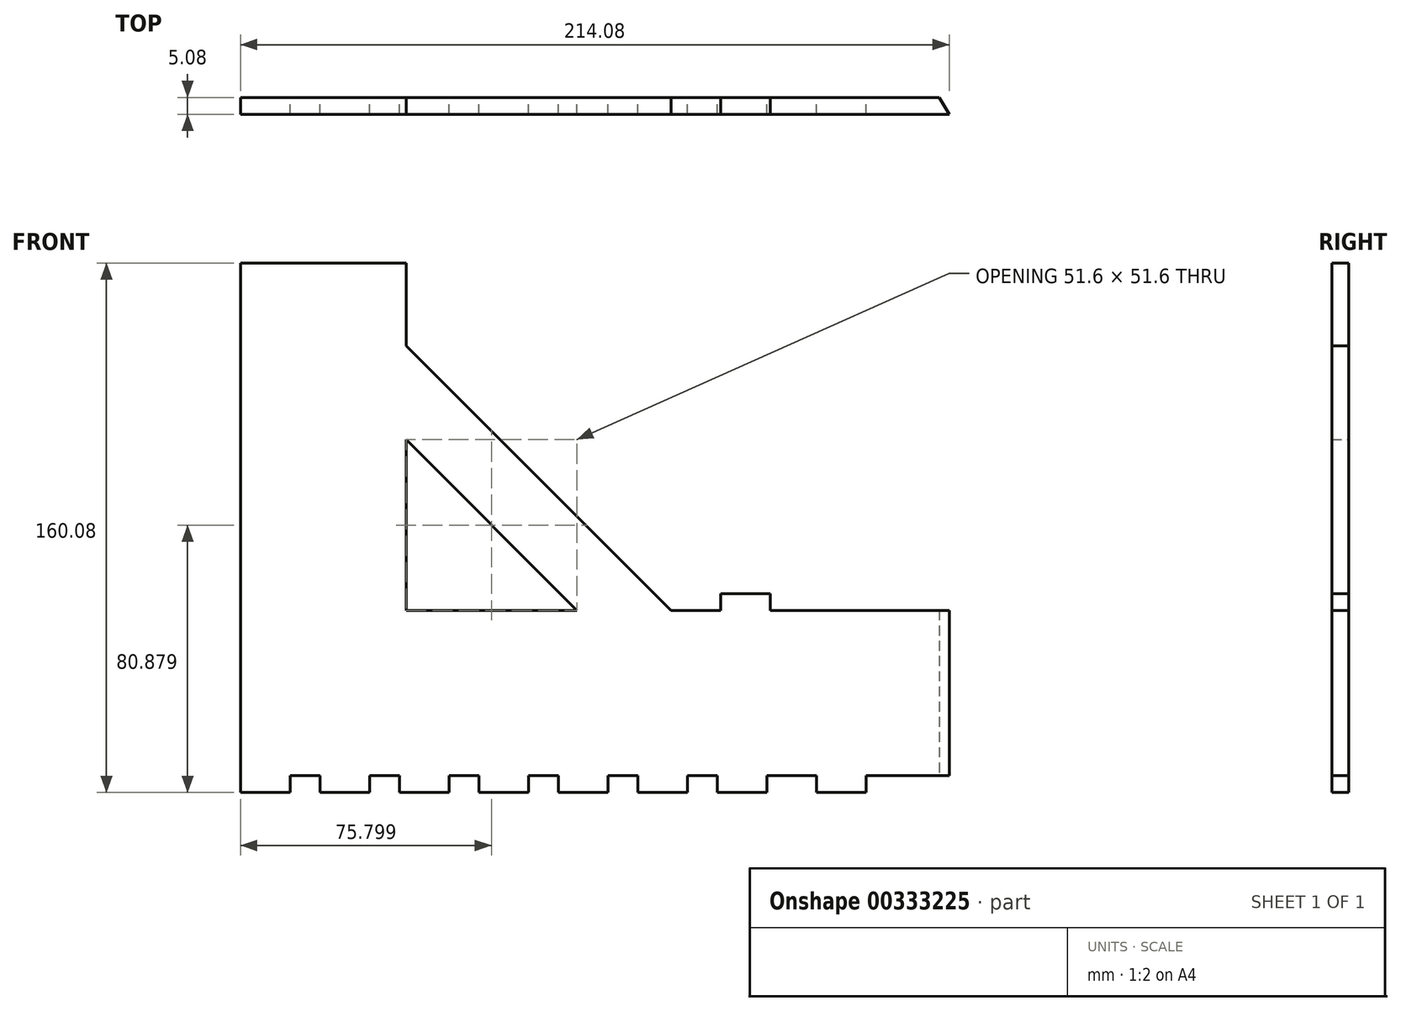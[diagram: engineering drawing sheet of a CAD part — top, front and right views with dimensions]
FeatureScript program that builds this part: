
annotation { "Feature Type Name" : "Feature", "Feature Type Description" : "" }
export const myFeature = defineFeature(function(context is Context, id is Id, definition is map)
    precondition{}
    {
        {
            var Q0;
            Q0=qCreatedBy(makeId("Front.planeOp"),FACE);
            var sketch = newSketch(context, id + "F0", { "sketchPlane" : qUnion([Q0])});
            skLineSegment(sketch, "E0", {"start": v(-32.42, 0) * mm, "end": v(-246.5, 0) * mm});
            skLineSegment(sketch, "E1", {"start": v(-246.5, 0) * mm, "end": v(-246.5, 130) * mm});
            skLineSegment(sketch, "E2", {"start": v(-246.5, 130) * mm, "end": v(-196.5, 130) * mm});
            skLineSegment(sketch, "E3", {"start": v(-196.5, 130) * mm, "end": v(-196.5, 50) * mm});
            skLineSegment(sketch, "E4", {"start": v(-196.5, 50) * mm, "end": v(-32.42, 50) * mm});
            skLineSegment(sketch, "E5", {"start": v(-196.5, 130) * mm, "end": v(-116.5, 50) * mm});
            skLineSegment(sketch, "E6", {"start": v(-196.5, 101.6) * mm, "end": v(-144.9, 50) * mm});
            skLineSegment(sketch, "E7", {"start": v(-246.5, 0) * mm, "end": v(-246.5, -5.08) * mm});
            skLineSegment(sketch, "E8", {"start": v(-246.5, -5.08) * mm, "end": v(-231.5, -5.08) * mm});
            skLineSegment(sketch, "E9", {"start": v(-231.5, -5.08) * mm, "end": v(-231.5, 0) * mm});
            skLineSegment(sketch, "E10.1.0.0", {"start": v(-207.5, -5.08) * mm, "end": v(-207.5, 0) * mm});
            skLineSegment(sketch, "E10.1.0.1", {"start": v(-222.5, -5.08) * mm, "end": v(-207.5, -5.08) * mm});
            skLineSegment(sketch, "E10.1.0.2", {"start": v(-222.5, 0) * mm, "end": v(-222.5, -5.08) * mm});
            skLineSegment(sketch, "E10.2.0.0", {"start": v(-183.5, -5.08) * mm, "end": v(-183.5, 0) * mm});
            skLineSegment(sketch, "E10.2.0.1", {"start": v(-198.5, -5.08) * mm, "end": v(-183.5, -5.08) * mm});
            skLineSegment(sketch, "E10.2.0.2", {"start": v(-198.5, 0) * mm, "end": v(-198.5, -5.08) * mm});
            skLineSegment(sketch, "E10.3.0.0", {"start": v(-159.5, -5.08) * mm, "end": v(-159.5, 0) * mm});
            skLineSegment(sketch, "E10.3.0.1", {"start": v(-174.5, -5.08) * mm, "end": v(-159.5, -5.08) * mm});
            skLineSegment(sketch, "E10.3.0.2", {"start": v(-174.5, 0) * mm, "end": v(-174.5, -5.08) * mm});
            skLineSegment(sketch, "E10.4.0.0", {"start": v(-135.5, -5.08) * mm, "end": v(-135.5, 0) * mm});
            skLineSegment(sketch, "E10.4.0.1", {"start": v(-150.5, -5.08) * mm, "end": v(-135.5, -5.08) * mm});
            skLineSegment(sketch, "E10.4.0.2", {"start": v(-150.5, 0) * mm, "end": v(-150.5, -5.08) * mm});
            skLineSegment(sketch, "E10.5.0.0", {"start": v(-111.5, -5.08) * mm, "end": v(-111.5, 0) * mm});
            skLineSegment(sketch, "E10.5.0.1", {"start": v(-126.5, -5.08) * mm, "end": v(-111.5, -5.08) * mm});
            skLineSegment(sketch, "E10.5.0.2", {"start": v(-126.5, 0) * mm, "end": v(-126.5, -5.08) * mm});
            skLineSegment(sketch, "E10.6.0.0", {"start": v(-87.5, -5.08) * mm, "end": v(-87.5, 0) * mm});
            skLineSegment(sketch, "E10.6.0.1", {"start": v(-102.5, -5.08) * mm, "end": v(-87.5, -5.08) * mm});
            skLineSegment(sketch, "E10.6.0.2", {"start": v(-102.5, 0) * mm, "end": v(-102.5, -5.08) * mm});
            skLineSegment(sketch, "E10.direction1", {"start": v(-246.5, -5.08) * mm, "end": v(-222.5, -5.08) * mm, "construction": true});
            skLineSegment(sketch, "E11", {"start": v(-32.42, 50) * mm, "end": v(-32.42, 0) * mm});
            skPoint(sketch, "E12.start.orphan", {"position": v(0, 50) * mm});
            skSolve(sketch);
        }
        {
            var Q0;
            Q0=qSketchRegion(id+"F0",true);
            extrude(context, id + "F1", {"entities" : qUnion([Q0]), "depth" : 5.08 * mm});
        }
        {
            var Q0;
            Q0=makeQuery(id+"F1.opExtrude","SWEPT_FACE",FACE,{"disambiguationData":[OSD([sQuery(id+"F0.wireOp",EDGE,"E2")])]});
            var Q1;
            Q1=makeQuery(id+"F1.opExtrude","SWEPT_FACE",FACE,{"disambiguationData":[OSD([sQuery(id+"F0.wireOp",EDGE,"0f3f7d79-0024-4810-854d-b7a6c9fa19c64.MirrorCS")])]});
            extrude(context, id + "F2", {"entities" : qUnion([Q0, Q1]), "operationType" : NewBodyOperationType.ADD, "depth" : 25 * mm});
        }
        {
            var Q0;
            {var subQ0=sQuery(id+"F0.wireOp",EDGE,"E0");Q0=makeQuery(id+"F1.opExtrude","SWEPT_FACE",FACE,{"disambiguationData":[OSD([subQ0]),TDD([makeQuery(id+"F0.imprint","IMPRINT",EDGE,{"disambiguationData":[TD([[makeQuery(id+"F0.imprint","INTERSECT",VERTEX,{"derivedFrom":[subQ0,sQuery(id+"F0.wireOp",EDGE,"E11")]}),-1.0]])],"derivedFrom":subQ0})])]});}
            var sketch = newSketch(context, id + "F3", { "sketchPlane" : qUnion([Q0])});
            skLineSegment(sketch, "E13", {"start": v(-32.42, 5.08) * mm, "end": v(-35.35, 0) * mm});
            skSolve(sketch);
        }
        {
            var Q0;
            {var subQ0=sQuery(id+"F3.wireOp",EDGE,"E13");Q0=makeQuery(id+"F3.imprint","IMPRINT",FACE,{"disambiguationData":[TD([[makeQuery(id+"F3.imprint","IMPRINT",EDGE,{"derivedFrom":subQ0}),1.0]])]});}
            extrude(context, id + "F4", {"entities" : qUnion([Q0]), "operationType" : NewBodyOperationType.REMOVE, "oppositeDirection" : true, "depth" : 58 * mm});
        }
        {
            var Q0;
            {var subQ0=sQuery(id+"F0.wireOp",EDGE,"E0");Q0=makeQuery(id+"F1.opExtrude","SWEPT_FACE",FACE,{"disambiguationData":[OSD([subQ0]),TDD([makeQuery(id+"F0.imprint","IMPRINT",EDGE,{"disambiguationData":[TD([[makeQuery(id+"F0.imprint","INTERSECT",VERTEX,{"derivedFrom":[subQ0,sQuery(id+"F0.wireOp",EDGE,"E11")]}),-1.0]])],"derivedFrom":subQ0})])]});}
            var sketch = newSketch(context, id + "F5", { "sketchPlane" : qUnion([Q0])});
            skLineSegment(sketch, "E14.bottom", {"start": v(-72.5, 5.08) * mm, "end": v(-57.5, 5.08) * mm});
            skLineSegment(sketch, "E14.top", {"start": v(-72.5, 0) * mm, "end": v(-57.5, 0) * mm});
            skLineSegment(sketch, "E14.right", {"start": v(-57.5, 5.08) * mm, "end": v(-57.5, 0) * mm});
            skLineSegment(sketch, "E15", {"start": v(-72.5, 5.08) * mm, "end": v(-72.5, 0) * mm});
            skPoint(sketch, "E14.left.start.orphan", {"position": v(-87.5, 5.08) * mm});
            skPoint(sketch, "E16.orphan", {"position": v(-87.5, 0) * mm});
            skSolve(sketch);
        }
        {
            var Q0;
            Q0=qSketchRegion(id+"F5",true);
            extrude(context, id + "F6", {"entities" : qUnion([Q0]), "operationType" : NewBodyOperationType.ADD, "depth" : 5.08 * mm});
        }
        {
            var Q0;
            {var subQ0=sQuery(id+"F0.wireOp",EDGE,"E4");Q0=makeQuery(id+"F1.opExtrude","SWEPT_FACE",FACE,{"disambiguationData":[OSD([subQ0]),TDD([makeQuery(id+"F0.imprint","IMPRINT",EDGE,{"disambiguationData":[TD([[makeQuery(id+"F0.imprint","INTERSECT",VERTEX,{"derivedFrom":[subQ0,sQuery(id+"F0.wireOp",EDGE,"E11")]}),1.0]])],"derivedFrom":subQ0})])]});}
            var sketch = newSketch(context, id + "F7", { "sketchPlane" : qUnion([Q0])});
            skLineSegment(sketch, "E17.bottom", {"start": v(-101.5, 0) * mm, "end": v(-86.5, 0) * mm});
            skLineSegment(sketch, "E17.top", {"start": v(-101.5, -5.08) * mm, "end": v(-86.5, -5.08) * mm});
            skLineSegment(sketch, "E17.right", {"start": v(-86.5, 0) * mm, "end": v(-86.5, -5.08) * mm});
            skLineSegment(sketch, "E18", {"start": v(-101.5, 0) * mm, "end": v(-101.5, -5.08) * mm});
            skPoint(sketch, "E17.left.start.orphan", {"position": v(-116.5, 0) * mm});
            skPoint(sketch, "E19.orphan", {"position": v(-116.5, -5.08) * mm});
            skSolve(sketch);
        }
        {
            var Q0;
            Q0=qSketchRegion(id+"F7",true);
            extrude(context, id + "F8", {"entities" : qUnion([Q0]), "operationType" : NewBodyOperationType.ADD, "depth" : 5.08 * mm});
        }
    });
